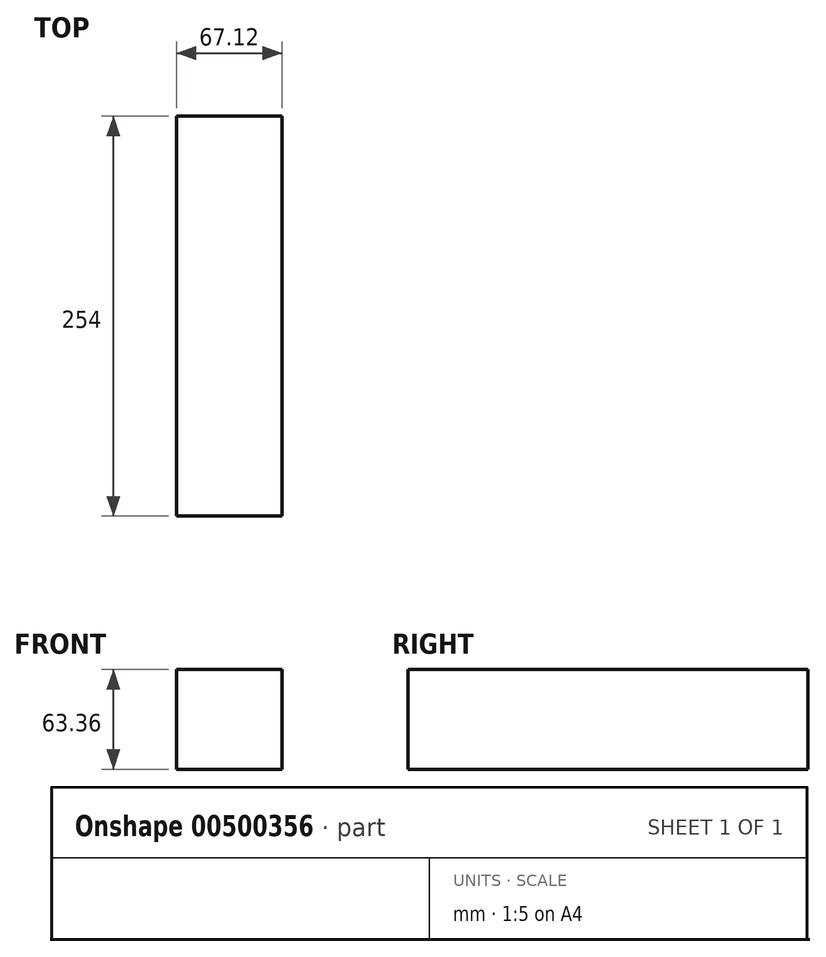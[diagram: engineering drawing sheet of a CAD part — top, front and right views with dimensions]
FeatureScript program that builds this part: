
annotation { "Feature Type Name" : "Feature", "Feature Type Description" : "" }
export const myFeature = defineFeature(function(context is Context, id is Id, definition is map)
    precondition{}
    {
        {
            var Q0;
            Q0=qCreatedBy(makeId("Front.planeOp"),FACE);
            var sketch = newSketch(context, id + "F0", { "sketchPlane" : qUnion([Q0])});
            skLineSegment(sketch, "E0.bottom", {"start": v(33.56, 31.68) * mm, "end": v(-33.56, 31.68) * mm});
            skLineSegment(sketch, "E0.top", {"start": v(33.56, -31.68) * mm, "end": v(-33.56, -31.68) * mm});
            skLineSegment(sketch, "E0.left", {"start": v(33.56, 31.68) * mm, "end": v(33.56, -31.68) * mm});
            skLineSegment(sketch, "E0.right", {"start": v(-33.56, 31.68) * mm, "end": v(-33.56, -31.68) * mm});
            skPoint(sketch, "E0.middle", {"position": v(0, 0) * mm});
            skSolve(sketch);
        }
        {
            var Q0;
            Q0 = qSketchRegion(id + "F0", true);
            extrude(context, id + "F1", {"entities" : qUnion([Q0]), "depth" : 254 * mm});
        }
    });
